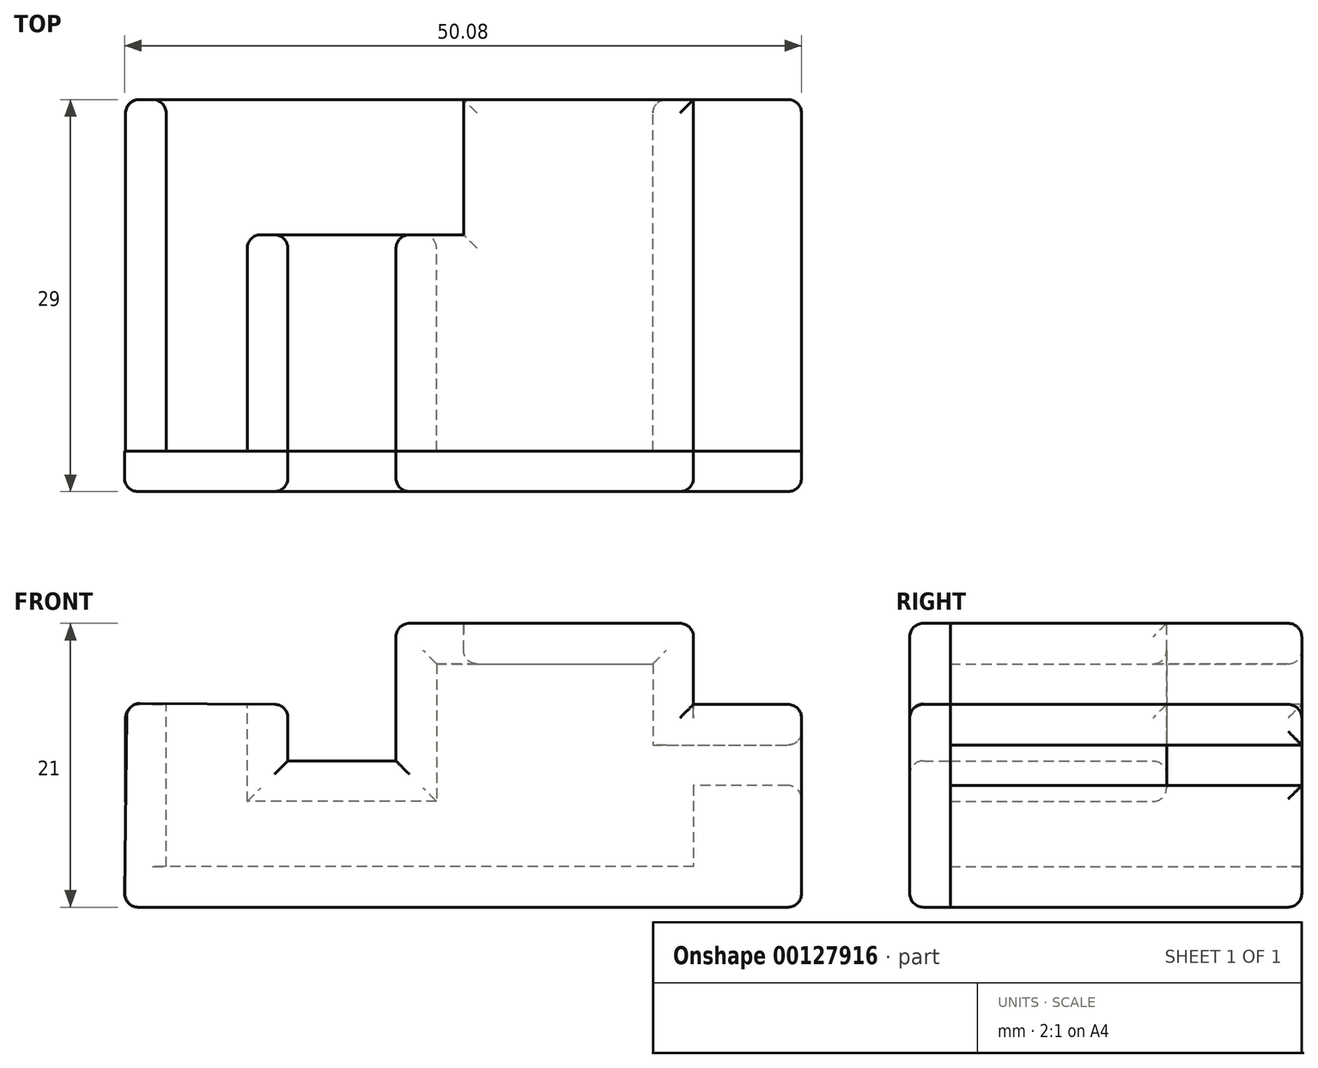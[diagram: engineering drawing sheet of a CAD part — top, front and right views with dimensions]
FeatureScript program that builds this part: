
annotation { "Feature Type Name" : "Feature", "Feature Type Description" : "" }
export const myFeature = defineFeature(function(context is Context, id is Id, definition is map)
    precondition{}
    {
        {
            var Q0;
            Q0=qCreatedBy(makeId("Front.planeOp"),FACE);
            var sketch = newSketch(context, id + "F0", { "sketchPlane" : qUnion([Q0])});
            skLineSegment(sketch, "E0", {"start": v(-50, 15) * mm, "end": v(-50, 0) * mm});
            skLineSegment(sketch, "E1", {"start": v(-50, 0) * mm, "end": v(0, 0) * mm});
            skLineSegment(sketch, "E2", {"start": v(0, 0) * mm, "end": v(0, 9) * mm});
            skLineSegment(sketch, "E3", {"start": v(0, 9) * mm, "end": v(-8, 9) * mm});
            skLineSegment(sketch, "E4", {"start": v(-8, 9) * mm, "end": v(-8, 3) * mm});
            skLineSegment(sketch, "E5", {"start": v(-8, 3) * mm, "end": v(-47, 3) * mm});
            skLineSegment(sketch, "E6", {"start": v(-47, 3) * mm, "end": v(-47, 15) * mm});
            skLineSegment(sketch, "E7", {"start": v(-47, 15) * mm, "end": v(-50, 15) * mm});
            skLineSegment(sketch, "E8", {"start": v(-41, 15) * mm, "end": v(-41, 7.82) * mm});
            skLineSegment(sketch, "E9", {"start": v(-41, 7.82) * mm, "end": v(-27, 7.82) * mm});
            skLineSegment(sketch, "E10", {"start": v(-27, 7.82) * mm, "end": v(-27, 18) * mm});
            skLineSegment(sketch, "E11", {"start": v(-27, 18) * mm, "end": v(-11, 18) * mm});
            skLineSegment(sketch, "E12", {"start": v(-11, 18) * mm, "end": v(-11, 12) * mm});
            skLineSegment(sketch, "E13", {"start": v(-11, 12) * mm, "end": v(0, 12) * mm});
            skLineSegment(sketch, "E14", {"start": v(0, 12) * mm, "end": v(0, 15) * mm});
            skLineSegment(sketch, "E15", {"start": v(-30, 21) * mm, "end": v(-30, 10.82) * mm});
            skLineSegment(sketch, "E16", {"start": v(-30, 10.82) * mm, "end": v(-38, 10.82) * mm});
            skLineSegment(sketch, "E17", {"start": v(-38, 10.82) * mm, "end": v(-38, 15) * mm});
            skLineSegment(sketch, "E18", {"start": v(-38, 15) * mm, "end": v(-41, 15) * mm});
            skLineSegment(sketch, "E19", {"start": v(-30, 21) * mm, "end": v(-8, 21) * mm});
            skLineSegment(sketch, "E20", {"start": v(-8, 21) * mm, "end": v(-8, 15) * mm});
            skLineSegment(sketch, "E21", {"start": v(-8, 15) * mm, "end": v(0, 15) * mm});
            skSolve(sketch);
        }
        {
            var Q0;
            Q0 = qSketchRegion(id + "F0", true);
            extrude(context, id + "F1", {"entities" : qUnion([Q0]), "endBound" : BoundingType.SYMMETRIC, "depth" : 26 * mm});
        }
        {
            var Q0;
            Q0=makeQuery(id+"F1.opExtrude","CAP_FACE",FACE,{"disambiguationData":[OSD([sQuery(id+"F0.wireOp",EDGE,"E0"),sQuery(id+"F0.wireOp",EDGE,"E1"),sQuery(id+"F0.wireOp",EDGE,"E2"),sQuery(id+"F0.wireOp",EDGE,"E3"),sQuery(id+"F0.wireOp",EDGE,"E4"),sQuery(id+"F0.wireOp",EDGE,"E5"),sQuery(id+"F0.wireOp",EDGE,"E6"),sQuery(id+"F0.wireOp",EDGE,"E7")])],"isStart":false});
            var sketch = newSketch(context, id + "F2", { "sketchPlane" : qUnion([Q0])});
            skLineSegment(sketch, "E22", {"start": v(-49.91, 15.1) * mm, "end": v(-38, 15) * mm});
            skLineSegment(sketch, "E23", {"start": v(-38, 15) * mm, "end": v(-38, 10.82) * mm});
            skLineSegment(sketch, "E24", {"start": v(-38, 10.82) * mm, "end": v(-30, 10.82) * mm});
            skLineSegment(sketch, "E25", {"start": v(-30, 10.82) * mm, "end": v(-30, 21) * mm});
            skLineSegment(sketch, "E26", {"start": v(-30, 21) * mm, "end": v(-8, 21) * mm});
            skLineSegment(sketch, "E27", {"start": v(-8, 21) * mm, "end": v(-8, 15) * mm});
            skLineSegment(sketch, "E28", {"start": v(-8, 15) * mm, "end": v(0, 15) * mm});
            skLineSegment(sketch, "E29", {"start": v(0, 15) * mm, "end": v(0, 0) * mm});
            skLineSegment(sketch, "E30", {"start": v(0, 0) * mm, "end": v(-50.1, 0) * mm});
            skLineSegment(sketch, "E31", {"start": v(-50.1, 0) * mm, "end": v(-49.91, 15.1) * mm});
            skSolve(sketch);
        }
        {
            var Q0;
            Q0 = qSketchRegion(id + "F2", true);
            extrude(context, id + "F3", {"entities" : qUnion([Q0]), "depth" : 3 * mm});
        }
        {
            var Q0;
            Q0=makeQuery(id+"F1.opExtrude","SWEPT_FACE",FACE,{"disambiguationData":[OSD([sQuery(id+"F0.wireOp",EDGE,"E19")])]});
            var sketch = newSketch(context, id + "F4", { "sketchPlane" : qUnion([Q0])});
            skLineSegment(sketch, "E32.bottom", {"start": v(-25, 13) * mm, "end": v(-47, 13) * mm});
            skLineSegment(sketch, "E32.top", {"start": v(-25, 3) * mm, "end": v(-47, 3) * mm});
            skLineSegment(sketch, "E32.left", {"start": v(-25, 13) * mm, "end": v(-25, 3) * mm});
            skLineSegment(sketch, "E32.right", {"start": v(-47, 13) * mm, "end": v(-47, 3) * mm});
            skSolve(sketch);
        }
        {
            var Q0;
            Q0 = qSketchRegion(id + "F4", true);
            var Q1;
            Q1=makeQuery(id+"F1.opExtrude","SWEPT_FACE",FACE,{"disambiguationData":[OSD([sQuery(id+"F0.wireOp",EDGE,"E5")])]});
            extrude(context, id + "F5", {"entities" : qUnion([Q0]), "operationType" : NewBodyOperationType.REMOVE, "endBound" : BoundingType.UP_TO_SURFACE, "oppositeDirection" : true, "endBoundEntityFace" : qUnion([Q1]), "depth" : 25 * mm});
        }
        {
            var Q0;
            Q0=makeQuery(id+"F1.opExtrude","SWEPT_EDGE",EDGE,{"disambiguationData":[OSD([sQuery(id+"F0.wireOp",EDGE,"E0"),sQuery(id+"F0.wireOp",EDGE,"E1")])]});
            var Q1;
            Q1=makeQuery(id+"F1.opExtrude","SWEPT_EDGE",EDGE,{"disambiguationData":[OSD([sQuery(id+"F0.wireOp",EDGE,"E17"),sQuery(id+"F0.wireOp",EDGE,"E18")])]});
            var Q2;
            Q2=makeQuery(id+"F3.opExtrude","SWEPT_EDGE",EDGE,{"disambiguationData":[OSD([sQuery(id+"F2.wireOp",EDGE,"E22"),sQuery(id+"F2.wireOp",EDGE,"E23")])]});
            var Q3;
            Q3=makeQuery(id+"F3.opExtrude","SWEPT_EDGE",EDGE,{"disambiguationData":[OSD([sQuery(id+"F2.wireOp",EDGE,"E22"),sQuery(id+"F2.wireOp",EDGE,"E31")])]});
            var Q4;
            Q4=makeQuery(id+"F3.opExtrude","CAP_EDGE",EDGE,{"disambiguationData":[OSD([sQuery(id+"F2.wireOp",EDGE,"E22")])],"isStart":false});
            var Q5;
            Q5=makeQuery(id+"F3.opExtrude","CAP_EDGE",EDGE,{"disambiguationData":[OSD([sQuery(id+"F2.wireOp",EDGE,"E31")])],"isStart":false});
            var Q6;
            Q6=makeQuery(id+"F3.opExtrude","SWEPT_EDGE",EDGE,{"disambiguationData":[OSD([sQuery(id+"F2.wireOp",EDGE,"E30"),sQuery(id+"F2.wireOp",EDGE,"E31")])]});
            var Q7;
            Q7=makeQuery(id+"F1.opExtrude","CAP_EDGE",EDGE,{"disambiguationData":[OSD([sQuery(id+"F0.wireOp",EDGE,"E1")])],"isStart":true});
            var Q8;
            Q8=makeQuery(id+"F1.opExtrude","CAP_EDGE",EDGE,{"disambiguationData":[OSD([sQuery(id+"F0.wireOp",EDGE,"E2")])],"isStart":true});
            var Q9;
            Q9=makeQuery(id+"F1.opExtrude","CAP_EDGE",EDGE,{"disambiguationData":[OSD([sQuery(id+"F0.wireOp",EDGE,"E14")])],"isStart":true});
            var Q10;
            Q10=makeQuery(id+"F1.opExtrude","SWEPT_EDGE",EDGE,{"disambiguationData":[OSD([sQuery(id+"F0.wireOp",EDGE,"E15"),sQuery(id+"F0.wireOp",EDGE,"E19")])]});
            var Q11;
            Q11=makeQuery(id+"F3.opExtrude","SWEPT_EDGE",EDGE,{"disambiguationData":[OSD([sQuery(id+"F2.wireOp",EDGE,"E25"),sQuery(id+"F2.wireOp",EDGE,"E26")])]});
            var Q12;
            Q12=makeQuery(id+"F1.opExtrude","SWEPT_EDGE",EDGE,{"disambiguationData":[OSD([sQuery(id+"F0.wireOp",EDGE,"E19"),sQuery(id+"F0.wireOp",EDGE,"E20")])]});
            var Q13;
            Q13=makeQuery(id+"F3.opExtrude","SWEPT_EDGE",EDGE,{"disambiguationData":[OSD([sQuery(id+"F2.wireOp",EDGE,"E26"),sQuery(id+"F2.wireOp",EDGE,"E27")])]});
            var Q14;
            Q14=makeQuery(id+"F3.opExtrude","CAP_EDGE",EDGE,{"disambiguationData":[OSD([sQuery(id+"F2.wireOp",EDGE,"E26")])],"isStart":false});
            var Q15;
            Q15=makeQuery(id+"F3.opExtrude","CAP_EDGE",EDGE,{"disambiguationData":[OSD([sQuery(id+"F2.wireOp",EDGE,"E25")])],"isStart":false});
            var Q16;
            Q16=makeQuery(id+"F3.opExtrude","CAP_EDGE",EDGE,{"disambiguationData":[OSD([sQuery(id+"F2.wireOp",EDGE,"E24")])],"isStart":false});
            var Q17;
            Q17=makeQuery(id+"F1.opExtrude","SWEPT_EDGE",EDGE,{"disambiguationData":[OSD([sQuery(id+"F0.wireOp",EDGE,"E14"),sQuery(id+"F0.wireOp",EDGE,"E21")])]});
            var Q18;
            Q18=makeQuery(id+"F3.opExtrude","SWEPT_EDGE",EDGE,{"disambiguationData":[OSD([sQuery(id+"F2.wireOp",EDGE,"E28"),sQuery(id+"F2.wireOp",EDGE,"E29")])]});
            var Q19;
            Q19=makeQuery(id+"F3.opExtrude","CAP_EDGE",EDGE,{"disambiguationData":[OSD([sQuery(id+"F2.wireOp",EDGE,"E30")])],"isStart":false});
            var Q20;
            Q20=makeQuery(id+"F3.opExtrude","CAP_EDGE",EDGE,{"disambiguationData":[OSD([sQuery(id+"F2.wireOp",EDGE,"E29")])],"isStart":false});
            var Q21;
            Q21=makeQuery(id+"F1.opExtrude","SWEPT_EDGE",EDGE,{"disambiguationData":[OSD([sQuery(id+"F0.wireOp",EDGE,"E1"),sQuery(id+"F0.wireOp",EDGE,"E2")])]});
            var Q22;
            Q22=makeQuery(id+"F3.opExtrude","SWEPT_EDGE",EDGE,{"disambiguationData":[OSD([sQuery(id+"F2.wireOp",EDGE,"E29"),sQuery(id+"F2.wireOp",EDGE,"E30")])]});
            var Q23;
            Q23=makeQuery(id+"F1.opExtrude","CAP_EDGE",EDGE,{"disambiguationData":[OSD([sQuery(id+"F0.wireOp",EDGE,"E19")])],"isStart":true});
            var Q24;
            Q24=makeQuery(id+"F1.opExtrude","CAP_EDGE",EDGE,{"disambiguationData":[OSD([sQuery(id+"F0.wireOp",EDGE,"E0")])],"isStart":true});
            var Q25;
            Q25=makeQuery(id+"F1.opExtrude","CAP_EDGE",EDGE,{"disambiguationData":[OSD([sQuery(id+"F0.wireOp",EDGE,"E21")])],"isStart":true});
            var Q26;
            Q26=makeQuery(id+"F5.boolean.opBoolean","COPY",EDGE,{"derivedFrom":makeQuery(id+"F5.opExtrude","CAP_EDGE",EDGE,{"disambiguationData":[OSD([sQuery(id+"F4.wireOp",EDGE,"E32.left")])],"isStart":true})});
            var Q27;
            Q27=makeQuery(id+"F5.boolean.opBoolean","INTERSECT",EDGE,{"derivedFrom":[makeQuery(id+"F1.opExtrude","SWEPT_FACE",FACE,{"disambiguationData":[OSD([sQuery(id+"F0.wireOp",EDGE,"E15")])]}),makeQuery(id+"F5.opExtrude","SWEPT_FACE",FACE,{"disambiguationData":[OSD([sQuery(id+"F4.wireOp",EDGE,"E32.top")])]})]});
            var Q28;
            Q28=makeQuery(id+"F5.boolean.opBoolean","INTERSECT",EDGE,{"derivedFrom":[makeQuery(id+"F1.opExtrude","SWEPT_FACE",FACE,{"disambiguationData":[OSD([sQuery(id+"F0.wireOp",EDGE,"E16")])]}),makeQuery(id+"F5.opExtrude","SWEPT_FACE",FACE,{"disambiguationData":[OSD([sQuery(id+"F4.wireOp",EDGE,"E32.top")])]})]});
            var Q29;
            Q29=makeQuery(id+"F5.boolean.opBoolean","COPY",EDGE,{"derivedFrom":makeQuery(id+"F5.opExtrude","CAP_EDGE",EDGE,{"disambiguationData":[OSD([sQuery(id+"F4.wireOp",EDGE,"E32.top")])],"isStart":true})});
            var Q30;
            Q30=makeQuery(id+"F1.opExtrude","SWEPT_EDGE",EDGE,{"disambiguationData":[OSD([sQuery(id+"F0.wireOp",EDGE,"E0"),sQuery(id+"F0.wireOp",EDGE,"E7")])]});
            var Q31;
            Q31=makeQuery(id+"F3.opExtrude","CAP_EDGE",EDGE,{"disambiguationData":[OSD([sQuery(id+"F2.wireOp",EDGE,"E28")])],"isStart":false});
            var Q32;
            Q32=makeQuery(id+"F3.opExtrude","CAP_EDGE",EDGE,{"disambiguationData":[OSD([sQuery(id+"F2.wireOp",EDGE,"E27")])],"isStart":false});
            var Q33;
            Q33=makeQuery(id+"F1.opExtrude","SWEPT_EDGE",EDGE,{"disambiguationData":[OSD([sQuery(id+"F0.wireOp",EDGE,"E13"),sQuery(id+"F0.wireOp",EDGE,"E14")])]});
            var Q34;
            Q34=makeQuery(id+"F1.opExtrude","SWEPT_EDGE",EDGE,{"disambiguationData":[OSD([sQuery(id+"F0.wireOp",EDGE,"E2"),sQuery(id+"F0.wireOp",EDGE,"E3")])]});
            var Q35;
            Q35=makeQuery(id+"F3.opExtrude","CAP_EDGE",EDGE,{"disambiguationData":[OSD([sQuery(id+"F2.wireOp",EDGE,"E23")])],"isStart":false});
            var Q36;
            Q36=makeQuery(id+"F5.boolean.opBoolean","INTERSECT",EDGE,{"derivedFrom":[makeQuery(id+"F1.opExtrude","SWEPT_FACE",FACE,{"disambiguationData":[OSD([sQuery(id+"F0.wireOp",EDGE,"E17")])]}),makeQuery(id+"F5.opExtrude","SWEPT_FACE",FACE,{"disambiguationData":[OSD([sQuery(id+"F4.wireOp",EDGE,"E32.top")])]})]});
            var Q37;
            Q37=makeQuery(id+"F1.opExtrude","CAP_EDGE",EDGE,{"disambiguationData":[OSD([sQuery(id+"F0.wireOp",EDGE,"E6")])],"isStart":true});
            var Q38;
            Q38=makeQuery(id+"F5.boolean.opBoolean","INTERSECT",EDGE,{"derivedFrom":[makeQuery(id+"F1.opExtrude","SWEPT_FACE",FACE,{"disambiguationData":[OSD([sQuery(id+"F0.wireOp",EDGE,"E8")])]}),makeQuery(id+"F5.opExtrude","SWEPT_FACE",FACE,{"disambiguationData":[OSD([sQuery(id+"F4.wireOp",EDGE,"E32.top")])]})]});
            var Q39;
            Q39=makeQuery(id+"F5.boolean.opBoolean","INTERSECT",EDGE,{"derivedFrom":[makeQuery(id+"F1.opExtrude","SWEPT_FACE",FACE,{"disambiguationData":[OSD([sQuery(id+"F0.wireOp",EDGE,"E10")])]}),makeQuery(id+"F5.opExtrude","SWEPT_FACE",FACE,{"disambiguationData":[OSD([sQuery(id+"F4.wireOp",EDGE,"E32.top")])]})]});
            var Q40;
            Q40=makeQuery(id+"F1.opExtrude","CAP_EDGE",EDGE,{"disambiguationData":[OSD([sQuery(id+"F0.wireOp",EDGE,"E12")])],"isStart":true});
            var Q41;
            Q41=makeQuery(id+"F1.opExtrude","CAP_EDGE",EDGE,{"disambiguationData":[OSD([sQuery(id+"F0.wireOp",EDGE,"E11")])],"isStart":true});
            var Q42;
            Q42=makeQuery(id+"F5.boolean.opBoolean","INTERSECT",EDGE,{"derivedFrom":[makeQuery(id+"F1.opExtrude","SWEPT_FACE",FACE,{"disambiguationData":[OSD([sQuery(id+"F0.wireOp",EDGE,"E11")])]}),makeQuery(id+"F5.opExtrude","SWEPT_FACE",FACE,{"disambiguationData":[OSD([sQuery(id+"F4.wireOp",EDGE,"E32.left")])]})]});
            var Q43;
            Q43=makeQuery(id+"F5.boolean.opBoolean","INTERSECT",EDGE,{"derivedFrom":[makeQuery(id+"F1.opExtrude","SWEPT_FACE",FACE,{"disambiguationData":[OSD([sQuery(id+"F0.wireOp",EDGE,"E11")])]}),makeQuery(id+"F5.opExtrude","SWEPT_FACE",FACE,{"disambiguationData":[OSD([sQuery(id+"F4.wireOp",EDGE,"E32.top")])]})]});
            var Q44;
            Q44=makeQuery(id+"F5.boolean.opBoolean","INTERSECT",EDGE,{"derivedFrom":[makeQuery(id+"F1.opExtrude","SWEPT_FACE",FACE,{"disambiguationData":[OSD([sQuery(id+"F0.wireOp",EDGE,"E9")])]}),makeQuery(id+"F5.opExtrude","SWEPT_FACE",FACE,{"disambiguationData":[OSD([sQuery(id+"F4.wireOp",EDGE,"E32.top")])]})]});
            fillet(context, id + "F6", {"entities" : qUnion([Q0, Q1, Q2, Q3, Q4, Q5, Q6, Q7, Q8, Q9, Q10, Q11, Q12, Q13, Q14, Q15, Q16, Q17, Q18, Q19, Q20, Q21, Q22, Q23, Q24, Q25, Q26, Q27, Q28, Q29, Q30, Q31, Q32, Q33, Q34, Q35, Q36, Q37, Q38, Q39, Q40, Q41, Q42, Q43, Q44]), "radius" : 1 * mm, "tangentPropagation" : true, "allowEdgeOverflow" : false});
        }
    });
